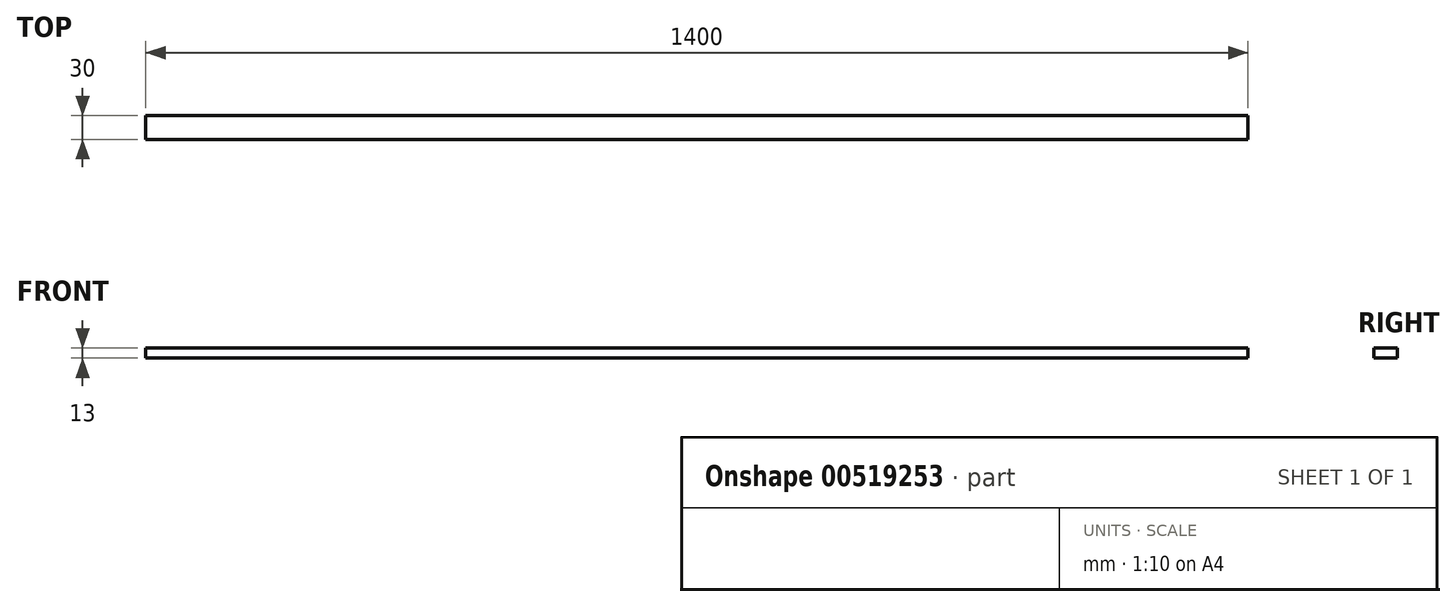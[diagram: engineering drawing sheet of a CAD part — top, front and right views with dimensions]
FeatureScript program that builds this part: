
annotation { "Feature Type Name" : "Feature", "Feature Type Description" : "" }
export const myFeature = defineFeature(function(context is Context, id is Id, definition is map)
    precondition{}
    {
        {
            var Q0;
            Q0=qCreatedBy(makeId("Right.planeOp"),FACE);
            var sketch = newSketch(context, id + "F0", { "sketchPlane" : qUnion([Q0])});
            skLineSegment(sketch, "E0.bottom", {"start": v(0, 0) * mm, "end": v(30, 0) * mm});
            skLineSegment(sketch, "E0.top", {"start": v(0, 13) * mm, "end": v(30, 13) * mm});
            skLineSegment(sketch, "E0.left", {"start": v(0, 0) * mm, "end": v(0, 13) * mm});
            skLineSegment(sketch, "E0.right", {"start": v(30, 0) * mm, "end": v(30, 13) * mm});
            skSolve(sketch);
        }
        {
            var Q0;
            Q0 = qSketchRegion(id + "F0", true);
            extrude(context, id + "F1", {"entities" : qUnion([Q0]), "oppositeDirection" : true, "depth" : 1400 * mm, "offsetDistance" : 25 * mm});
        }
    });
